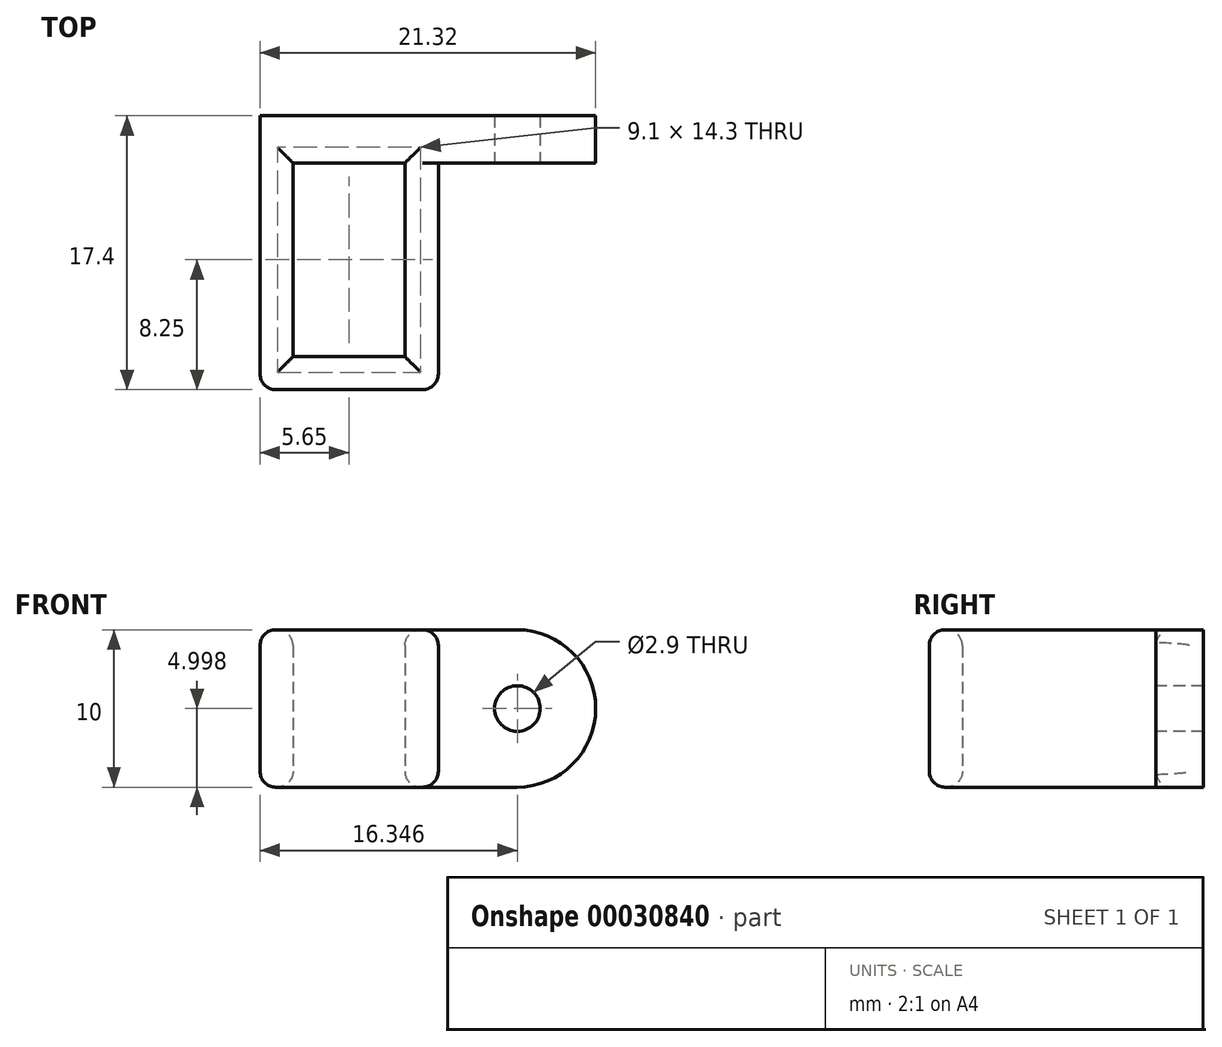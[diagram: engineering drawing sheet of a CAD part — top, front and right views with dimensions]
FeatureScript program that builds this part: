
annotation { "Feature Type Name" : "Feature", "Feature Type Description" : "" }
export const myFeature = defineFeature(function(context is Context, id is Id, definition is map)
    precondition{}
    {
        {
            var Q0;
            Q0=qCreatedBy(makeId("Top.planeOp"),FACE);
            var sketch = newSketch(context, id + "F0", { "sketchPlane" : qUnion([Q0])});
            skLineSegment(sketch, "E0", {"start": v(0, 0) * mm, "end": v(0, 12.3) * mm});
            skLineSegment(sketch, "E1", {"start": v(0, 12.3) * mm, "end": v(7.1, 12.3) * mm});
            skLineSegment(sketch, "E2", {"start": v(7.1, 12.3) * mm, "end": v(7.1, 0) * mm});
            skLineSegment(sketch, "E3", {"start": v(7.1, 0) * mm, "end": v(0, 0) * mm});
            skLineSegment(sketch, "E4", {"start": v(-2.1, 0) * mm, "end": v(-2.1, 12.3) * mm});
            skLineSegment(sketch, "E5", {"start": v(-2.1, 12.3) * mm, "end": v(-2.08, 12.3) * mm});
            skLineSegment(sketch, "E6", {"start": v(-2.1, 0) * mm, "end": v(-2.1, -2.1) * mm});
            skLineSegment(sketch, "E7", {"start": v(-2.1, -2.1) * mm, "end": v(7.1, -2.1) * mm});
            skLineSegment(sketch, "E8", {"start": v(7.1, -2.1) * mm, "end": v(9.22, -2.1) * mm});
            skLineSegment(sketch, "E9", {"start": v(9.22, -2.1) * mm, "end": v(9.22, 12.3) * mm});
            skLineSegment(sketch, "E10", {"start": v(9.22, 12.3) * mm, "end": v(9.22, 15.3) * mm});
            skLineSegment(sketch, "E11", {"start": v(-2.1, 14.4) * mm, "end": v(-2.08, 12.2) * mm});
            skLineSegment(sketch, "E12", {"start": v(-2.1, 14.4) * mm, "end": v(-2.1, 17.4) * mm});
            skLineSegment(sketch, "E13", {"start": v(9.22, 15.3) * mm, "end": v(19.22, 15.3) * mm});
            skLineSegment(sketch, "E14", {"start": v(-2.1, 17.4) * mm, "end": v(19.22, 17.4) * mm});
            skLineSegment(sketch, "E15", {"start": v(19.22, 17.4) * mm, "end": v(19.22, 15.3) * mm});
            skLineSegment(sketch, "E16", {"start": v(9.22, 12.3) * mm, "end": v(19.22, 12.3) * mm});
            skLineSegment(sketch, "E17", {"start": v(19.22, 12.3) * mm, "end": v(19.22, 15.3) * mm});
            skLineSegment(sketch, "E18", {"start": v(9.22, 15.3) * mm, "end": v(-2.1, 15.3) * mm});
            skSolve(sketch);
        }
        {
            var Q0;
            Q0=makeQuery(id+"F0.imprint","IMPRINT",FACE,{"disambiguationData":[TD([[makeQuery(id+"F0.imprint","IMPRINT",EDGE,{"derivedFrom":sQuery(id+"F0.wireOp",EDGE,"E10")}),-1.0]])]});
            var Q1;
            Q1=makeQuery(id+"F0.imprint","IMPRINT",FACE,{"disambiguationData":[TD([[makeQuery(id+"F0.imprint","IMPRINT",EDGE,{"derivedFrom":sQuery(id+"F0.wireOp",EDGE,"E0")}),1.0]])]});
            var Q2;
            Q2=makeQuery(id+"F0.imprint","IMPRINT",FACE,{"disambiguationData":[TD([[makeQuery(id+"F0.imprint","IMPRINT",EDGE,{"derivedFrom":sQuery(id+"F0.wireOp",EDGE,"E0")}),1.0]])]});
            extrude(context, id + "F1", {"entities" : qUnion([Q0, Q1, Q2]), "depth" : 10 * mm});
        }
        {
            var Q0;
            Q0=qCreatedBy(makeId("Front.planeOp"),FACE);
            var sketch = newSketch(context, id + "F2", { "sketchPlane" : qUnion([Q0])});
            skCircle(sketch, "E19", {"center": v(14.25, 5) * mm, "radius": 1.45 * mm});
            skPoint(sketch, "E20.orphan", {"position": v(19.25, 5) * mm});
            skPoint(sketch, "E21.orphan", {"position": v(14.25, 10) * mm});
            skPoint(sketch, "E22.orphan", {"position": v(19.25, 10) * mm});
            skPoint(sketch, "E23.orphan", {"position": v(9.24, 5) * mm});
            skPoint(sketch, "E24.right.start.orphan", {"position": v(9.24, 10) * mm});
            skPoint(sketch, "E25.orphan", {"position": v(14.25, 0) * mm});
            skPoint(sketch, "E26.orphan", {"position": v(19.25, 0) * mm});
            skPoint(sketch, "E24.top.end.orphan", {"position": v(9.24, 0) * mm});
            skSolve(sketch);
        }
        {
            var Q0;
            Q0=makeQuery(id+"F2.imprint","IMPRINT",FACE,{"disambiguationData":[TD([[makeQuery(id+"F2.imprint","IMPRINT",EDGE,{"derivedFrom":sQuery(id+"F2.wireOp",EDGE,"E19")}),1.0]])]});
            var Q1;
            Q1=makeQuery(id+"F1.opExtrude","SWEPT_FACE",FACE,{"disambiguationData":[OSD([sQuery(id+"F0.wireOp",EDGE,"E13"),sQuery(id+"F0.wireOp",EDGE,"E18")])]});
            var Q2;
            Q2=makeQuery(id+"F1.opExtrude","SWEPT_FACE",FACE,{"disambiguationData":[OSD([sQuery(id+"F0.wireOp",EDGE,"E14")])]});
            extrude(context, id + "F3", {"entities" : qUnion([Q0, Q1]), "operationType" : NewBodyOperationType.REMOVE, "endBound" : BoundingType.THROUGH_ALL, "oppositeDirection" : true, "endBoundEntityFace" : qUnion([Q2]), "depth" : 25 * mm});
        }
        {
            var Q0;
            Q0=makeQuery(id+"F1.opExtrude","CAP_EDGE",EDGE,{"disambiguationData":[OSD([sQuery(id+"F0.wireOp",EDGE,"E17")])],"isStart":false});
            var Q1;
            Q1=makeQuery(id+"F1.opExtrude","CAP_EDGE",EDGE,{"disambiguationData":[OSD([sQuery(id+"F0.wireOp",EDGE,"E17")])],"isStart":true});
            fillet(context, id + "F4", {"entities" : qUnion([Q0, Q1]), "radius" : 5 * mm, "tangentPropagation" : true, "allowEdgeOverflow" : false});
        }
        {
            var Q0;
            Q0=makeQuery(id+"F1.opExtrude","CAP_EDGE",EDGE,{"disambiguationData":[OSD([sQuery(id+"F0.wireOp",EDGE,"E9"),sQuery(id+"F0.wireOp",EDGE,"E10")])],"isStart":false});
            var Q1;
            Q1=makeQuery(id+"F1.opExtrude","SWEPT_EDGE",EDGE,{"disambiguationData":[OSD([sQuery(id+"F0.wireOp",EDGE,"E8"),sQuery(id+"F0.wireOp",EDGE,"E9")])]});
            var Q2;
            Q2=makeQuery(id+"F1.opExtrude","CAP_EDGE",EDGE,{"disambiguationData":[OSD([sQuery(id+"F0.wireOp",EDGE,"E9"),sQuery(id+"F0.wireOp",EDGE,"E10")])],"isStart":true});
            var Q3;
            Q3=makeQuery(id+"F1.opExtrude","CAP_EDGE",EDGE,{"disambiguationData":[OSD([sQuery(id+"F0.wireOp",EDGE,"E7"),sQuery(id+"F0.wireOp",EDGE,"E8")])],"isStart":true});
            var Q4;
            Q4=makeQuery(id+"F1.opExtrude","SWEPT_EDGE",EDGE,{"disambiguationData":[OSD([sQuery(id+"F0.wireOp",EDGE,"E6"),sQuery(id+"F0.wireOp",EDGE,"E7")])]});
            var Q5;
            Q5=makeQuery(id+"F1.opExtrude","CAP_EDGE",EDGE,{"disambiguationData":[OSD([sQuery(id+"F0.wireOp",EDGE,"E7"),sQuery(id+"F0.wireOp",EDGE,"E8")])],"isStart":false});
            var Q6;
            Q6=makeQuery(id+"F1.opExtrude","CAP_EDGE",EDGE,{"disambiguationData":[OSD([sQuery(id+"F0.wireOp",EDGE,"E4"),sQuery(id+"F0.wireOp",EDGE,"E6")])],"isStart":false});
            var Q7;
            Q7=makeQuery(id+"F1.opExtrude","CAP_EDGE",EDGE,{"disambiguationData":[OSD([sQuery(id+"F0.wireOp",EDGE,"E4"),sQuery(id+"F0.wireOp",EDGE,"E6")])],"isStart":true});
            var Q8;
            Q8=makeQuery(id+"F1.opExtrude","CAP_EDGE",EDGE,{"disambiguationData":[OSD([sQuery(id+"F0.wireOp",EDGE,"E2")])],"isStart":true});
            var Q9;
            Q9=makeQuery(id+"F1.opExtrude","CAP_EDGE",EDGE,{"disambiguationData":[OSD([sQuery(id+"F0.wireOp",EDGE,"E0")])],"isStart":true});
            var Q10;
            Q10=makeQuery(id+"F1.opExtrude","CAP_EDGE",EDGE,{"disambiguationData":[OSD([sQuery(id+"F0.wireOp",EDGE,"E3")])],"isStart":true});
            var Q11;
            Q11=makeQuery(id+"F1.opExtrude","CAP_EDGE",EDGE,{"disambiguationData":[OSD([sQuery(id+"F0.wireOp",EDGE,"E1")])],"isStart":true});
            var Q12;
            Q12=makeQuery(id+"F1.opExtrude","CAP_EDGE",EDGE,{"disambiguationData":[OSD([sQuery(id+"F0.wireOp",EDGE,"E1")])],"isStart":false});
            var Q13;
            Q13=makeQuery(id+"F1.opExtrude","CAP_EDGE",EDGE,{"disambiguationData":[OSD([sQuery(id+"F0.wireOp",EDGE,"E2")])],"isStart":false});
            var Q14;
            Q14=makeQuery(id+"F1.opExtrude","CAP_EDGE",EDGE,{"disambiguationData":[OSD([sQuery(id+"F0.wireOp",EDGE,"E0")])],"isStart":false});
            var Q15;
            Q15=makeQuery(id+"F1.opExtrude","CAP_EDGE",EDGE,{"disambiguationData":[OSD([sQuery(id+"F0.wireOp",EDGE,"E3")])],"isStart":false});
            var Q16;
            Q16=makeQuery(id+"F4.opFillet","BLEND_EDGE",EDGE,{"blendedFrom":[makeQuery(id+"F1.opExtrude","CAP_EDGE",EDGE,{"disambiguationData":[OSD([sQuery(id+"F0.wireOp",EDGE,"E15")])],"isStart":false}),makeQuery(id+"F1.opExtrude","SWEPT_FACE",FACE,{"disambiguationData":[OSD([sQuery(id+"F0.wireOp",EDGE,"E13")])]})],"blendedInto":[makeQuery(id+"F1.opExtrude","SWEPT_FACE",FACE,{"disambiguationData":[OSD([sQuery(id+"F0.wireOp",EDGE,"E13")])]})]});
            fillet(context, id + "F5", {"entities" : qUnion([Q0, Q1, Q2, Q3, Q4, Q5, Q6, Q7, Q8, Q9, Q10, Q11, Q12, Q13, Q14, Q15, Q16]), "radius" : 1 * mm, "tangentPropagation" : true, "allowEdgeOverflow" : false});
        }
    });
